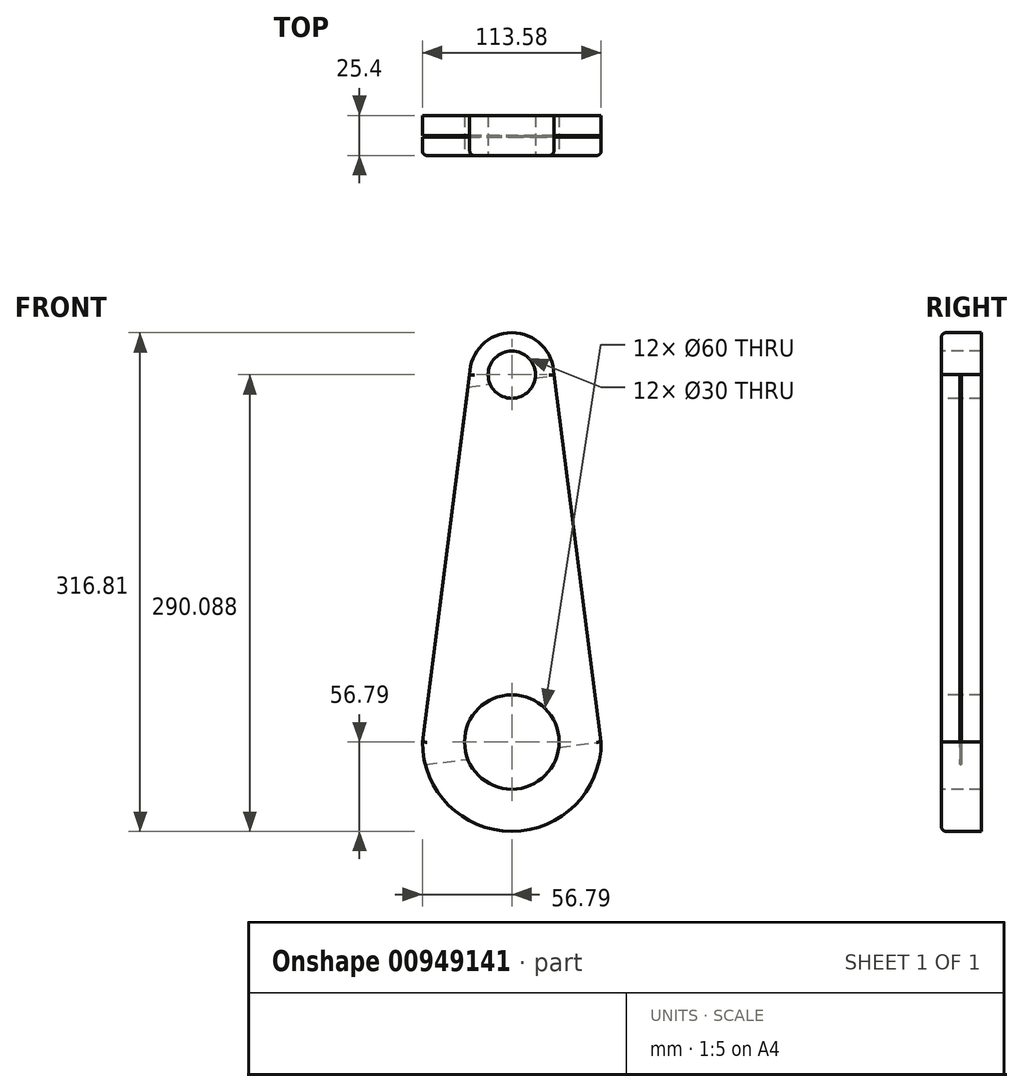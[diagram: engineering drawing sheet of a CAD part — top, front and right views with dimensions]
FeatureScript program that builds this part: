
annotation { "Feature Type Name" : "Feature", "Feature Type Description" : "" }
export const myFeature = defineFeature(function(context is Context, id is Id, definition is map)
    precondition{}
    {
        {
            var Q0;
            Q0=qCreatedBy(makeId("Front.planeOp"),FACE);
            var sketch = newSketch(context, id + "F0", { "sketchPlane" : qUnion([Q0])});
            skLineSegment(sketch, "E0.bottom", {"start": v(57.3, 66.07) * mm, "end": v(42.9, 66.07) * mm});
            skLineSegment(sketch, "E0.top", {"start": v(57.3, 70.66) * mm, "end": v(42.9, 70.66) * mm});
            skLineSegment(sketch, "E0.left", {"start": v(57.3, 66.07) * mm, "end": v(57.3, 70.66) * mm});
            skLineSegment(sketch, "E0.right", {"start": v(42.9, 66.07) * mm, "end": v(42.9, 70.66) * mm});
            skLineSegment(sketch, "E1.bottom", {"start": v(42.9, 43.77) * mm, "end": v(59.2, 43.77) * mm});
            skLineSegment(sketch, "E1.top", {"start": v(42.9, 56.61) * mm, "end": v(59.2, 56.61) * mm});
            skLineSegment(sketch, "E1.left", {"start": v(42.9, 43.77) * mm, "end": v(42.9, 56.61) * mm});
            skLineSegment(sketch, "E1.right", {"start": v(59.2, 43.77) * mm, "end": v(59.2, 56.61) * mm});
            skLineSegment(sketch, "E2.bottom", {"start": v(57.3, 66.07) * mm, "end": v(44, 66.07) * mm});
            skLineSegment(sketch, "E2.top", {"start": v(57.3, 76.6) * mm, "end": v(44, 76.6) * mm});
            skLineSegment(sketch, "E2.left", {"start": v(57.3, 66.07) * mm, "end": v(57.3, 76.6) * mm});
            skLineSegment(sketch, "E2.right", {"start": v(44, 66.07) * mm, "end": v(44, 76.6) * mm});
            skLineSegment(sketch, "E3.bottom", {"start": v(57.3, 70.66) * mm, "end": v(53.36, 70.66) * mm});
            skLineSegment(sketch, "E3.top", {"start": v(57.3, 76.6) * mm, "end": v(53.36, 76.6) * mm});
            skLineSegment(sketch, "E3.left", {"start": v(57.3, 70.66) * mm, "end": v(57.3, 76.6) * mm});
            skLineSegment(sketch, "E3.right", {"start": v(53.36, 70.66) * mm, "end": v(53.36, 76.6) * mm});
            skSolve(sketch);
        }
        {
            var Q0;
            Q0 = qSketchRegion(id + "F0", true);
            var Q1;
            Q1=makeQuery(id+"F0.imprint","IMPRINT",FACE,{"disambiguationData":[TD([[makeQuery(id+"F0.imprint","IMPRINT",EDGE,{"derivedFrom":sQuery(id+"F0.wireOp",EDGE,"E1.bottom")}),1.0]])]});
            extrude(context, id + "F1", {"entities" : qUnion([Q0, Q1]), "depth" : 25.4 * mm, "offsetDistance" : 25.4 * mm});
        }
        {
            var Q0;
            Q0=makeQuery(id+"F1.opExtrude","SWEPT_BODY",BODY,{"disambiguationData":[OSD([sQuery(id+"F0.wireOp",EDGE,"E0.bottom"),sQuery(id+"F0.wireOp",EDGE,"E0.top"),sQuery(id+"F0.wireOp",EDGE,"E0.right"),sQuery(id+"F0.wireOp",EDGE,"E2.bottom"),sQuery(id+"F0.wireOp",EDGE,"E2.top"),sQuery(id+"F0.wireOp",EDGE,"E2.left"),sQuery(id+"F0.wireOp",EDGE,"E2.right"),sQuery(id+"F0.wireOp",EDGE,"E3.top"),sQuery(id+"F0.wireOp",EDGE,"E3.left")])]});
            deleteBodies(context, id + "F2", {"entities" : qUnion([Q0])});
        }
        {
            var Q0;
            Q0=makeQuery(id+"F1.opExtrude","SWEPT_BODY",BODY,{"disambiguationData":[OSD([sQuery(id+"F0.wireOp",EDGE,"E1.bottom"),sQuery(id+"F0.wireOp",EDGE,"E1.top"),sQuery(id+"F0.wireOp",EDGE,"E1.left"),sQuery(id+"F0.wireOp",EDGE,"E1.right")])]});
            deleteBodies(context, id + "F3", {"entities" : qUnion([Q0])});
        }
        {
            var Q0;
            Q0=qCreatedBy(makeId("Front.planeOp"),FACE);
            var sketch = newSketch(context, id + "F4", { "sketchPlane" : qUnion([Q0])});
            skArc(sketch, "E4", {"start": v(-54.93, 14.4) * mm, "mid": v(0, -56.79) * mm, "end": v(54.93, 14.4) * mm});
            skArc(sketch, "E5", {"start": v(26.72, 233.3) * mm, "mid": v(0, 260.02) * mm, "end": v(-26.72, 233.3) * mm});
            skLineSegment(sketch, "E6", {"start": v(0, 233.3) * mm, "end": v(0, 0) * mm});
            skLineSegment(sketch, "E7", {"start": v(56.79, 0) * mm, "end": v(26.72, 233.3) * mm});
            skLineSegment(sketch, "E8.MirrorCS", {"start": v(-56.79, 0) * mm, "end": v(-26.72, 233.3) * mm});
            skSolve(sketch);
        }
        {
            var Q0;
            {var subQ3=sQuery(id+"F4.wireOp",EDGE,"E5");Q0=makeQuery(id+"F4.imprint","IMPRINT",FACE,{"disambiguationData":[TD([[makeQuery(id+"F4.imprint","IMPRINT",EDGE,{"derivedFrom":subQ3}),1.0]])]});}
            extrude(context, id + "F5", {"entities" : qUnion([Q0]), "depth" : 25.4 * mm, "offsetDistance" : 25.4 * mm});
        }
        {
            var Q0;
            Q0=makeQuery(id+"F5.opExtrude","CAP_FACE",FACE,{"disambiguationData":[OSD([sQuery(id+"F4.wireOp",EDGE,"E4"),sQuery(id+"F4.wireOp",EDGE,"E5"),sQuery(id+"F4.wireOp",EDGE,"E7"),sQuery(id+"F4.wireOp",EDGE,"E8.MirrorCS")])],"isStart":false});
            var sketch = newSketch(context, id + "F6", { "sketchPlane" : qUnion([Q0])});
            skCircle(sketch, "E9", {"center": v(0, 0) * mm, "radius": 30 * mm});
            skSolve(sketch);
        }
        {
            var Q0;
            Q0=makeQuery(id+"F6.imprint","IMPRINT",FACE,{"disambiguationData":[TD([[makeQuery(id+"F6.imprint","IMPRINT",EDGE,{"derivedFrom":sQuery(id+"F6.wireOp",EDGE,"E9")}),1.0]])]});
            extrude(context, id + "F7", {"entities" : qUnion([Q0]), "operationType" : NewBodyOperationType.REMOVE, "endBound" : BoundingType.THROUGH_ALL, "oppositeDirection" : true, "depth" : 25 * mm, "offsetDistance" : 25 * mm});
        }
        {
            var Q0;
            Q0=makeQuery(id+"F5.opExtrude","SWEPT_FACE",FACE,{"disambiguationData":[OSD([sQuery(id+"F4.wireOp",EDGE,"E7")])]});
            var sketch = newSketch(context, id + "F8", { "sketchPlane" : qUnion([Q0])});
            skLineSegment(sketch, "E10.bottom", {"start": v(-13.8, 227.3) * mm, "end": v(-12.7, 227.3) * mm});
            skLineSegment(sketch, "E10.top", {"start": v(-13.8, -7.26) * mm, "end": v(-12.7, -7.26) * mm});
            skLineSegment(sketch, "E10.left", {"start": v(-13.8, 227.3) * mm, "end": v(-13.8, -7.26) * mm});
            skLineSegment(sketch, "E10.right", {"start": v(-12.7, 227.3) * mm, "end": v(-12.7, -7.26) * mm});
            skSolve(sketch);
        }
        {
            var Q0;
            Q0=makeQuery(id+"F8.imprint","IMPRINT",FACE,{"disambiguationData":[TD([[makeQuery(id+"F8.imprint","IMPRINT",EDGE,{"derivedFrom":sQuery(id+"F8.wireOp",EDGE,"E10.bottom")}),-1.0]])]});
            extrude(context, id + "F9", {"entities" : qUnion([Q0]), "operationType" : NewBodyOperationType.REMOVE, "endBound" : BoundingType.THROUGH_ALL, "oppositeDirection" : true, "depth" : 25 * mm, "offsetDistance" : 25 * mm});
        }
        {
            var Q0;
            Q0=makeQuery(id+"F5.opExtrude","CAP_FACE",FACE,{"disambiguationData":[OSD([sQuery(id+"F4.wireOp",EDGE,"E4"),sQuery(id+"F4.wireOp",EDGE,"E5"),sQuery(id+"F4.wireOp",EDGE,"E7"),sQuery(id+"F4.wireOp",EDGE,"E8.MirrorCS")])],"isStart":false});
            var sketch = newSketch(context, id + "F10", { "sketchPlane" : qUnion([Q0])});
            skCircle(sketch, "E11", {"center": v(0, 233.3) * mm, "radius": 15 * mm});
            skSolve(sketch);
        }
        {
            var Q0;
            Q0=sQuery(id+"F10.wireOp",VERTEX,"E11.center");
            var Q1;
            Q1=makeQuery(id+"F5.opExtrude","SWEPT_BODY",BODY,{"disambiguationData":[OSD([sQuery(id+"F4.wireOp",EDGE,"E4"),sQuery(id+"F4.wireOp",EDGE,"E5"),sQuery(id+"F4.wireOp",EDGE,"E7"),sQuery(id+"F4.wireOp",EDGE,"E8.MirrorCS")])]});
            hole(context, id + "F11", {"style" : HoleStyle.SIMPLE, "endStyle" : HoleEndStyle.THROUGH, "holeDiameter" : 30 * mm, "majorDiameter" : 5 * mm, "isTappedThrough" : true, "tappedDepth" : 12 * mm, "tapClearance" : 3, "locations" : qUnion([Q0]), "scope" : qUnion([Q1])});
        }
        {
            var Q0;
            Q0=makeQuery(id+"F5.opExtrude","CAP_EDGE",EDGE,{"disambiguationData":[OSD([sQuery(id+"F4.wireOp",EDGE,"E8.MirrorCS")])],"isStart":false});
            var Q1;
            Q1=makeQuery(id+"F5.opExtrude","CAP_EDGE",EDGE,{"disambiguationData":[OSD([sQuery(id+"F4.wireOp",EDGE,"E7")])],"isStart":false});
            var Q2;
            Q2=makeQuery(id+"F5.opExtrude","CAP_EDGE",EDGE,{"disambiguationData":[OSD([sQuery(id+"F4.wireOp",EDGE,"E5")])],"isStart":false});
            var Q3;
            Q3=makeQuery(id+"F5.opExtrude","CAP_EDGE",EDGE,{"disambiguationData":[OSD([sQuery(id+"F4.wireOp",EDGE,"E4")])],"isStart":false});
            var Q4;
            Q4=makeQuery(id+"F7.boolean.opBoolean","COPY",EDGE,{"derivedFrom":makeQuery(id+"F7.opExtrude","CAP_EDGE",EDGE,{"disambiguationData":[OSD([sQuery(id+"F6.wireOp",EDGE,"E9")])],"isStart":true})});
            fillet(context, id + "F12", {"entities" : qUnion([Q0, Q1, Q2, Q3, Q4]), "radius" : 3 * mm, "tangentPropagation" : true, "allowEdgeOverflow" : false});
        }
    });
